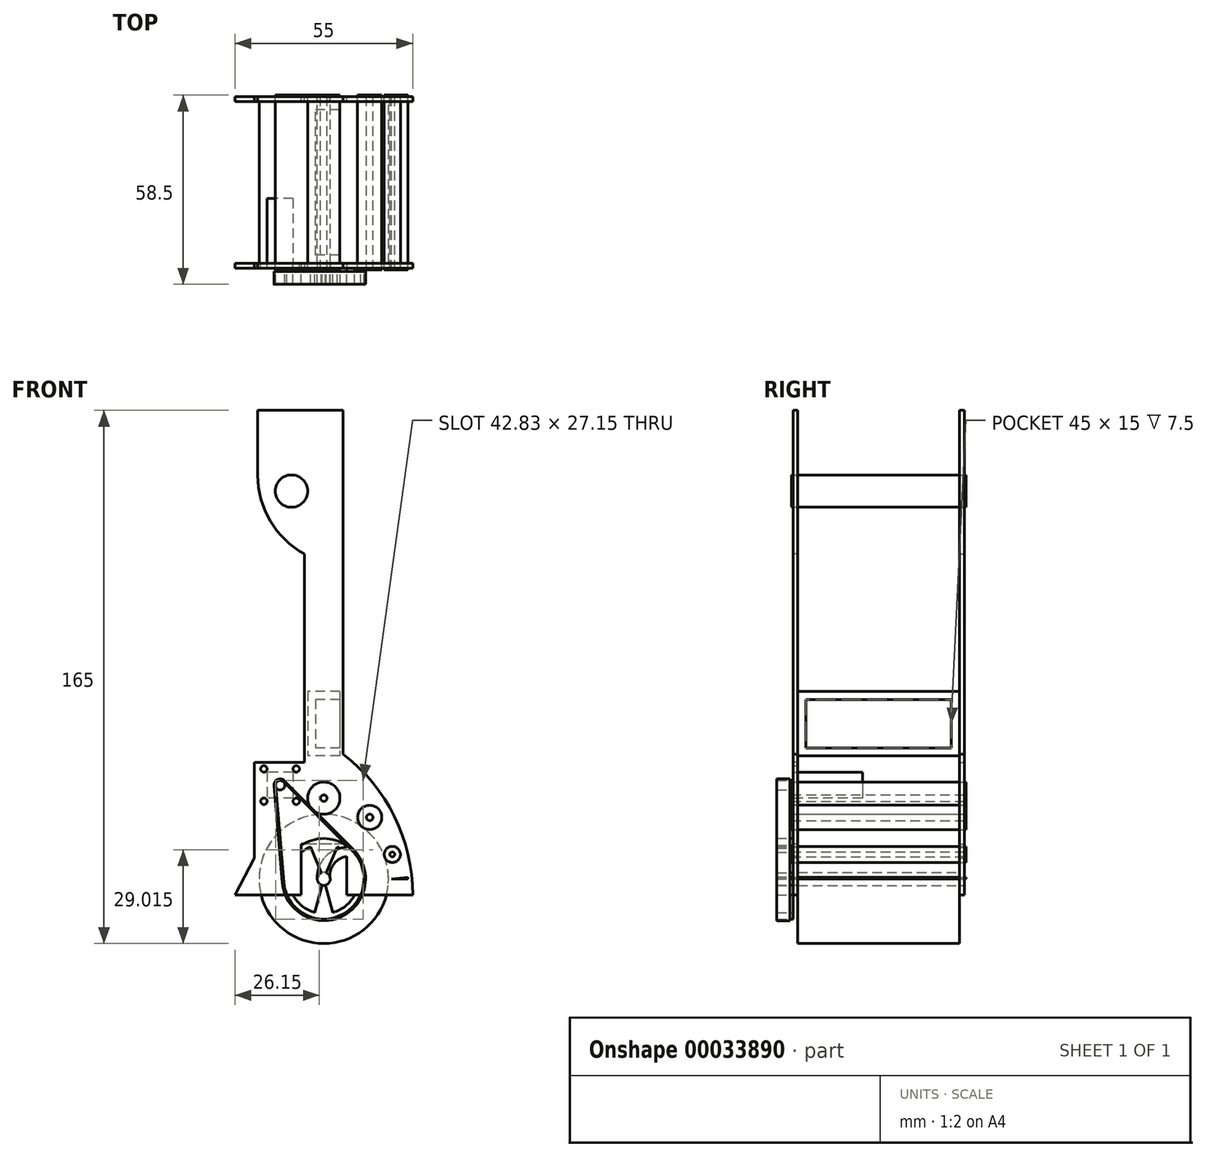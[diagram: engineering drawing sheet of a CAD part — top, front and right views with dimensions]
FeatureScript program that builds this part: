
annotation { "Feature Type Name" : "Feature", "Feature Type Description" : "" }
export const myFeature = defineFeature(function(context is Context, id is Id, definition is map)
    precondition{}
    {
        {
            var Q0;
            Q0=qCreatedBy(makeId("Front.planeOp"),FACE);
            var sketch = newSketch(context, id + "F0", { "sketchPlane" : qUnion([Q0])});
            skCircle(sketch, "E0", {"center": v(0, 0) * mm, "radius": 20 * mm});
            skCircle(sketch, "E1", {"center": v(0, 0) * mm, "radius": 2 * mm});
            skSolve(sketch);
        }
        {
            var Q0;
            Q0=makeQuery(id+"F0.imprint","IMPRINT",FACE,{"disambiguationData":[TD([[makeQuery(id+"F0.imprint","IMPRINT",EDGE,{"derivedFrom":sQuery(id+"F0.wireOp",EDGE,"E0")}),1.0]])]});
            extrude(context, id + "F1", {"entities" : qUnion([Q0]), "endBound" : BoundingType.SYMMETRIC, "depth" : 50 * mm});
        }
        {
            var Q0;
            Q0=qCreatedBy(makeId("Front.planeOp"),FACE);
            var sketch = newSketch(context, id + "F2", { "sketchPlane" : qUnion([Q0])});
            skCircle(sketch, "E2", {"center": v(0, 25) * mm, "radius": 5 * mm});
            skCircle(sketch, "E3", {"center": v(14.2, 19.04) * mm, "radius": 3.75 * mm});
            skCircle(sketch, "E4", {"center": v(21.18, 7.58) * mm, "radius": 2.5 * mm});
            skLineSegment(sketch, "E5", {"start": v(21, 0) * mm, "end": v(26, 0.44) * mm});
            skLineSegment(sketch, "E6", {"start": v(26, 0.44) * mm, "end": v(26, 0) * mm});
            skLineSegment(sketch, "E7", {"start": v(26, 0) * mm, "end": v(21, 0) * mm});
            skCircle(sketch, "E8", {"center": v(0, 25) * mm, "radius": 1 * mm});
            skCircle(sketch, "E9", {"center": v(14.2, 19.04) * mm, "radius": 1 * mm});
            skCircle(sketch, "E10", {"center": v(21.18, 7.58) * mm, "radius": 0.75 * mm});
            skCircle(sketch, "E11", {"center": v(-10, 120) * mm, "radius": 5 * mm});
            skPoint(sketch, "E12.center.orphan", {"position": v(0, 120) * mm});
            skSolve(sketch);
        }
        {
            var Q0;
            Q0=makeQuery(id+"F2.imprint","IMPRINT",FACE,{"disambiguationData":[TD([[makeQuery(id+"F2.imprint","IMPRINT",EDGE,{"derivedFrom":sQuery(id+"F2.wireOp",EDGE,"E2")}),1.0]])]});
            var Q1;
            Q1=makeQuery(id+"F2.imprint","IMPRINT",FACE,{"disambiguationData":[TD([[makeQuery(id+"F2.imprint","IMPRINT",EDGE,{"derivedFrom":sQuery(id+"F2.wireOp",EDGE,"E3")}),1.0]])]});
            var Q2;
            Q2=makeQuery(id+"F2.imprint","IMPRINT",FACE,{"disambiguationData":[TD([[makeQuery(id+"F2.imprint","IMPRINT",EDGE,{"derivedFrom":sQuery(id+"F2.wireOp",EDGE,"E4")}),1.0]])]});
            var Q3;
            Q3=makeQuery(id+"F2.imprint","IMPRINT",FACE,{"disambiguationData":[TD([[makeQuery(id+"F2.imprint","IMPRINT",EDGE,{"derivedFrom":sQuery(id+"F2.wireOp",EDGE,"E5")}),-1.0]])]});
            var Q4;
            Q4=makeQuery(id+"F2.imprint","IMPRINT",FACE,{"disambiguationData":[TD([[makeQuery(id+"F2.imprint","IMPRINT",EDGE,{"derivedFrom":sQuery(id+"F2.wireOp",EDGE,"E11")}),1.0]])]});
            extrude(context, id + "F3", {"entities" : qUnion([Q0, Q1, Q2, Q3, Q4]), "operationType" : NewBodyOperationType.ADD, "endBound" : BoundingType.SYMMETRIC, "depth" : 54 * mm});
        }
        {
            var Q0;
            Q0=qCreatedBy(makeId("Right.planeOp"),FACE);
            var sketch = newSketch(context, id + "F4", { "sketchPlane" : qUnion([Q0])});
            skLineSegment(sketch, "E13.top", {"start": v(-25, 145) * mm, "end": v(-26.5, 145) * mm});
            skLineSegment(sketch, "E13.left", {"start": v(-25, -5) * mm, "end": v(-25, 145) * mm});
            skLineSegment(sketch, "E13.right", {"start": v(-26.5, -5) * mm, "end": v(-26.5, 145) * mm});
            skLineSegment(sketch, "E14", {"start": v(-26.5, -5) * mm, "end": v(-25, -5) * mm});
            skSolve(sketch);
        }
        {
            var Q0;
            Q0=makeQuery(id+"F4.imprint","IMPRINT",FACE,{"disambiguationData":[TD([[makeQuery(id+"F4.imprint","IMPRINT",EDGE,{"derivedFrom":sQuery(id+"F4.wireOp",EDGE,"E13.bottom")}),-1.0]])]});
            var Q1;
            Q1=makeQuery(id+"F4.imprint","IMPRINT",FACE,{"disambiguationData":[TD([[makeQuery(id+"F4.imprint","IMPRINT",EDGE,{"derivedFrom":sQuery(id+"F4.wireOp",EDGE,"E13.top")}),1.0]])]});
            extrude(context, id + "F5", {"entities" : qUnion([Q0, Q1]), "endBound" : BoundingType.SYMMETRIC, "depth" : 55 * mm});
        }
        {
            var Q0;
            Q0=makeQuery(id+"F5.opExtrude","SWEPT_FACE",FACE,{"disambiguationData":[OSD([sQuery(id+"F4.wireOp",EDGE,"E13.right")])]});
            var sketch = newSketch(context, id + "F6", { "sketchPlane" : qUnion([Q0])});
            skLineSegment(sketch, "E15", {"start": v(-82.98, 0) * mm, "end": v(0, 0) * mm, "construction": true});
            skLineSegment(sketch, "E16", {"start": v(-6, 36.03) * mm, "end": v(-6, 100.52) * mm});
            skLineSegment(sketch, "E17", {"start": v(0, 0) * mm, "end": v(0, 66.1) * mm, "construction": true});
            skLineSegment(sketch, "E18", {"start": v(-20.41, 145) * mm, "end": v(-20.41, 124.89) * mm});
            skLineSegment(sketch, "E19", {"start": v(-20.41, 145) * mm, "end": v(6, 145) * mm});
            skLineSegment(sketch, "E20", {"start": v(-27.5, -5) * mm, "end": v(-21.52, 6.42) * mm});
            skLineSegment(sketch, "E21", {"start": v(6, 145) * mm, "end": v(6, 38.62) * mm});
            skArc(sketch, "E22", {"start": v(-20.41, 124.89) * mm, "mid": v(-16.54, 110.73) * mm, "end": v(-6, 100.52) * mm});
            skArc(sketch, "E23", {"start": v(27.5, -5) * mm, "mid": v(21.83, 19.32) * mm, "end": v(6, 38.62) * mm});
            skArc(sketch, "E24", {"start": v(-2, 0) * mm, "mid": v(0, -2) * mm, "end": v(2, 0) * mm});
            skLineSegment(sketch, "E25.trimOffspring", {"start": v(2, 0) * mm, "end": v(98.38, 0) * mm, "construction": true});
            skLineSegment(sketch, "E26", {"start": v(7.08, 0) * mm, "end": v(7.08, 6.96) * mm});
            skLineSegment(sketch, "E27", {"start": v(7.08, 10.84) * mm, "end": v(-6.96, 10.84) * mm});
            skLineSegment(sketch, "E28", {"start": v(-6.96, 10.84) * mm, "end": v(-6.96, 0) * mm});
            skArc(sketch, "E29", {"start": v(7.08, 6.96) * mm, "mid": v(3.06, 4.56) * mm, "end": v(2, 0) * mm});
            skArc(sketch, "E30", {"start": v(7.08, 9.77) * mm, "mid": v(0.47, 6.81) * mm, "end": v(-2, 0) * mm});
            skLineSegment(sketch, "E31", {"start": v(-6.96, 0) * mm, "end": v(-6.96, -5) * mm});
            skLineSegment(sketch, "E32", {"start": v(-6.96, -5) * mm, "end": v(7.08, -5) * mm});
            skLineSegment(sketch, "E33", {"start": v(7.08, 0) * mm, "end": v(7.08, -5) * mm});
            skLineSegment(sketch, "E34.trimOffspring", {"start": v(7.08, 9.77) * mm, "end": v(7.08, 10.84) * mm});
            skLineSegment(sketch, "E35", {"start": v(-6, 36.03) * mm, "end": v(-21.52, 36.03) * mm});
            skLineSegment(sketch, "E36", {"start": v(-21.52, 36.03) * mm, "end": v(-21.52, 6.42) * mm});
            skSolve(sketch);
        }
        {
            var Q0;
            Q0=makeQuery(id+"F6.imprint","IMPRINT",FACE,{"disambiguationData":[TD([[makeQuery(id+"F6.imprint","IMPRINT",EDGE,{"derivedFrom":sQuery(id+"F6.wireOp",EDGE,"E16")}),1.0]])]});
            var Q1;
            {var subQ2=sQuery(id+"F6.wireOp",EDGE,"E21");Q1=makeQuery(id+"F6.imprint","IMPRINT",FACE,{"disambiguationData":[TD([[makeQuery(id+"F6.imprint","IMPRINT",EDGE,{"derivedFrom":subQ2}),1.0]])]});}
            var Q2;
            Q2=makeQuery(id+"F6.imprint","IMPRINT",FACE,{"disambiguationData":[TD([[makeQuery(id+"F6.imprint","IMPRINT",EDGE,{"derivedFrom":sQuery(id+"F6.wireOp",EDGE,"E24")}),-1.0]])]});
            extrude(context, id + "F7", {"entities" : qUnion([Q0, Q1, Q2]), "operationType" : NewBodyOperationType.REMOVE, "oppositeDirection" : true, "depth" : 1.5 * mm});
        }
        {
            var Q0;
            Q0=makeQuery(id+"F5.opExtrude","SWEPT_BODY",BODY,{"disambiguationData":[OSD([sQuery(id+"F4.wireOp",EDGE,"E13.bottom"),sQuery(id+"F4.wireOp",EDGE,"E13.top"),sQuery(id+"F4.wireOp",EDGE,"E13.left"),sQuery(id+"F4.wireOp",EDGE,"E13.right")])]});
            var Q1;
            Q1=qCreatedBy(makeId("Front.planeOp"),FACE);
            mirror(context, id + "F8", {"entities" : qUnion([Q0]), "mirrorPlane" : qUnion([Q1])});
        }
        {
            var Q0;
            Q0=makeQuery(id+"F5.opExtrude","SWEPT_FACE",FACE,{"disambiguationData":[OSD([sQuery(id+"F4.wireOp",EDGE,"E13.left")])]});
            var sketch = newSketch(context, id + "F9", { "sketchPlane" : qUnion([Q0])});
            skCircle(sketch, "E37", {"center": v(8.52, 34.03) * mm, "radius": 1 * mm});
            skCircle(sketch, "E38", {"center": v(18.52, 34.03) * mm, "radius": 1 * mm});
            skCircle(sketch, "E39", {"center": v(8.52, 24.03) * mm, "radius": 1 * mm});
            skCircle(sketch, "E40", {"center": v(18.52, 24.03) * mm, "radius": 1 * mm});
            skLineSegment(sketch, "E41", {"start": v(18.52, 34.03) * mm, "end": v(18.52, 24.03) * mm, "construction": true});
            skLineSegment(sketch, "E42", {"start": v(8.52, 34.03) * mm, "end": v(8.52, 24.03) * mm, "construction": true});
            skLineSegment(sketch, "E43.bottom", {"start": v(9.52, 33.03) * mm, "end": v(17.52, 33.03) * mm});
            skLineSegment(sketch, "E43.top", {"start": v(9.52, 25.03) * mm, "end": v(17.52, 25.03) * mm});
            skLineSegment(sketch, "E43.left", {"start": v(9.52, 33.03) * mm, "end": v(9.52, 25.03) * mm});
            skLineSegment(sketch, "E43.right", {"start": v(17.52, 33.03) * mm, "end": v(17.52, 25.03) * mm});
            skLineSegment(sketch, "E44", {"start": v(8.52, 34.03) * mm, "end": v(18.52, 34.03) * mm, "construction": true});
            skSolve(sketch);
        }
        {
            var Q0;
            Q0=makeQuery(id+"F9.imprint","IMPRINT",FACE,{"disambiguationData":[TD([[makeQuery(id+"F9.imprint","IMPRINT",EDGE,{"derivedFrom":sQuery(id+"F9.wireOp",EDGE,"E43.bottom")}),-1.0]])]});
            extrude(context, id + "F10", {"entities" : qUnion([Q0]), "depth" : 20 * mm});
        }
        {
            var Q0;
            Q0=makeQuery(id+"F9.imprint","IMPRINT",FACE,{"disambiguationData":[TD([[makeQuery(id+"F9.imprint","IMPRINT",EDGE,{"derivedFrom":sQuery(id+"F9.wireOp",EDGE,"E37")}),-1.0]])]});
            var sketch = newSketch(context, id + "F11", { "sketchPlane" : qUnion([Q0])});
            skCircle(sketch, "E45", {"center": v(8.52, 34.03) * mm, "radius": 1 * mm});
            skCircle(sketch, "E46", {"center": v(18.52, 34.03) * mm, "radius": 1 * mm});
            skCircle(sketch, "E47", {"center": v(8.52, 24.03) * mm, "radius": 1 * mm});
            skCircle(sketch, "E48", {"center": v(18.52, 24.03) * mm, "radius": 1 * mm});
            skSolve(sketch);
        }
        {
            var Q0;
            Q0 = qSketchRegion(id + "F11", true);
            extrude(context, id + "F12", {"entities" : qUnion([Q0]), "operationType" : NewBodyOperationType.REMOVE, "endBound" : BoundingType.THROUGH_ALL, "oppositeDirection" : true, "depth" : 25 * mm});
        }
        {
            var Q0;
            Q0=makeQuery(id+"F5.opExtrude","SWEPT_FACE",FACE,{"disambiguationData":[OSD([sQuery(id+"F4.wireOp",EDGE,"E13.right")])]});
            var sketch = newSketch(context, id + "F13", { "sketchPlane" : qUnion([Q0])});
            skCircle(sketch, "E49", {"center": v(-13.52, 29.03) * mm, "radius": 1.5 * mm});
            skLineSegment(sketch, "E50", {"start": v(-18.52, 24.03) * mm, "end": v(-8.52, 34.03) * mm, "construction": true});
            skLineSegment(sketch, "E51", {"start": v(-18.52, 34.03) * mm, "end": v(-8.52, 24.03) * mm, "construction": true});
            skCircle(sketch, "E52", {"center": v(0, 0) * mm, "radius": 12.5 * mm});
            skArc(sketch, "E53", {"start": v(-4.11, 9.93) * mm, "mid": v(-10.73, -0.69) * mm, "end": v(-2.82, -10.38) * mm});
            skCircle(sketch, "E54", {"center": v(0, 0) * mm, "radius": 2.01 * mm});
            skLineSegment(sketch, "E55", {"start": v(0.77, 1.86) * mm, "end": v(4.11, 9.93) * mm});
            skLineSegment(sketch, "E56", {"start": v(-0.77, 1.86) * mm, "end": v(-4.11, 9.93) * mm});
            skLineSegment(sketch, "E57", {"start": v(-0.52, -1.93) * mm, "end": v(-2.82, -10.38) * mm});
            skLineSegment(sketch, "E58", {"start": v(0.52, -1.93) * mm, "end": v(2.82, -10.38) * mm});
            skLineSegment(sketch, "E59", {"start": v(0, 0) * mm, "end": v(0, 9.4) * mm, "construction": true});
            skArc(sketch, "E60.trimOffspring", {"start": v(2.82, -10.38) * mm, "mid": v(10.73, -0.69) * mm, "end": v(4.11, 9.93) * mm});
            skSolve(sketch);
        }
        {
            var Q0;
            Q0=makeQuery(id+"F13.imprint","IMPRINT",FACE,{"disambiguationData":[TD([[makeQuery(id+"F13.imprint","IMPRINT",EDGE,{"derivedFrom":sQuery(id+"F13.wireOp",EDGE,"E49")}),1.0]])]});
            var Q1;
            {var subQ2=sQuery(id+"F6.wireOp",EDGE,"E28");var subQ3=sQuery(id+"F6.wireOp",EDGE,"E31");var subQ7=sQuery(id+"F13.wireOp",EDGE,"E52");var subQ9=makeQuery(id+"F7.boolean.opBoolean","COPY",EDGE,{"derivedFrom":makeQuery(id+"F7.opExtrude","CAP_EDGE",EDGE,{"disambiguationData":[OSD([subQ2,subQ3])],"isStart":true})});var subQ11=makeQuery(id+"F13.imprint","INTERSECT",VERTEX,{"derivedFrom":[subQ9,subQ7]});Q1=makeQuery(id+"F13.imprint","IMPRINT",FACE,{"disambiguationData":[TD([[makeQuery(id+"F13.imprint","IMPRINT",EDGE,{"disambiguationData":[TD([[subQ11,-1.0]])],"derivedFrom":subQ9}),-1.0]])]});}
            var Q2;
            {var subQ16=sQuery(id+"F13.wireOp",EDGE,"E54");var subQ18=sQuery(id+"F13.wireOp",EDGE,"E57");var subQ19=makeQuery(id+"F13.imprint","INTERSECT",VERTEX,{"derivedFrom":[subQ16,subQ18]});Q2=makeQuery(id+"F13.imprint","IMPRINT",FACE,{"disambiguationData":[TD([[makeQuery(id+"F13.imprint","IMPRINT",EDGE,{"disambiguationData":[TD([[subQ19,-1.0]])],"derivedFrom":subQ16}),-1.0]])]});}
            var Q3;
            {var subQ7=makeQuery(id+"F7.boolean.opBoolean","COPY",EDGE,{"derivedFrom":makeQuery(id+"F7.opExtrude","CAP_EDGE",EDGE,{"disambiguationData":[OSD([sQuery(id+"F6.wireOp",EDGE,"E34.trimOffspring")])],"isStart":true})});var subQ9=makeQuery(id+"F7.boolean.opBoolean","COPY",EDGE,{"derivedFrom":makeQuery(id+"F7.opExtrude","CAP_EDGE",EDGE,{"disambiguationData":[OSD([sQuery(id+"F6.wireOp",EDGE,"E30")])],"isStart":true})});var subQ10=makeQuery(id+"F13.imprint","INTERSECT",VERTEX,{"derivedFrom":[subQ9,subQ7]});Q3=makeQuery(id+"F13.imprint","IMPRINT",FACE,{"disambiguationData":[TD([[makeQuery(id+"F13.imprint","IMPRINT",EDGE,{"disambiguationData":[TD([[subQ10,-1.0]])],"derivedFrom":subQ9}),1.0]])]});}
            var Q4;
            {var subQ0=makeQuery(id+"F7.boolean.opBoolean","COPY",EDGE,{"derivedFrom":makeQuery(id+"F7.opExtrude","CAP_EDGE",EDGE,{"disambiguationData":[OSD([sQuery(id+"F6.wireOp",EDGE,"E27")])],"isStart":true})});var subQ1=sQuery(id+"F13.wireOp",EDGE,"E52");var subQ3=makeQuery(id+"F13.imprint","INTERSECT",VERTEX,{"disambiguationData":[OD(0.0)],"derivedFrom":[subQ0,subQ1]});Q4=makeQuery(id+"F13.imprint","IMPRINT",FACE,{"disambiguationData":[TD([[makeQuery(id+"F13.imprint","IMPRINT",EDGE,{"disambiguationData":[TD([[subQ3,-1.0]])],"derivedFrom":subQ1}),1.0]])]});}
            var Q5;
            {var subQ6=sQuery(id+"F13.wireOp",EDGE,"E52");var subQ16=makeQuery(id+"F7.boolean.opBoolean","COPY",EDGE,{"derivedFrom":makeQuery(id+"F7.opExtrude","CAP_EDGE",EDGE,{"disambiguationData":[OSD([sQuery(id+"F6.wireOp",EDGE,"E27")])],"isStart":true})});var subQ18=makeQuery(id+"F13.imprint","INTERSECT",VERTEX,{"disambiguationData":[OD(0.0)],"derivedFrom":[subQ16,subQ6]});Q5=makeQuery(id+"F13.imprint","IMPRINT",FACE,{"disambiguationData":[TD([[makeQuery(id+"F13.imprint","IMPRINT",EDGE,{"disambiguationData":[TD([[subQ18,1.0]])],"derivedFrom":subQ6}),1.0]])]});}
            var Q6;
            {var subQ3=sQuery(id+"F13.wireOp",EDGE,"E55");var subQ5=sQuery(id+"F13.wireOp",EDGE,"E54");var subQ7=makeQuery(id+"F13.imprint","INTERSECT",VERTEX,{"derivedFrom":[subQ5,subQ3]});Q6=makeQuery(id+"F13.imprint","IMPRINT",FACE,{"disambiguationData":[TD([[makeQuery(id+"F13.imprint","IMPRINT",EDGE,{"disambiguationData":[TD([[subQ7,-1.0]])],"derivedFrom":subQ5}),-1.0]])]});}
            var Q7;
            {var subQ1=sQuery(id+"F13.wireOp",EDGE,"E54");var subQ11=makeQuery(id+"F13.imprint","INTERSECT",VERTEX,{"derivedFrom":[subQ1,sQuery(id+"F13.wireOp",EDGE,"E55")]});Q7=makeQuery(id+"F13.imprint","IMPRINT",FACE,{"disambiguationData":[TD([[makeQuery(id+"F13.imprint","IMPRINT",EDGE,{"disambiguationData":[TD([[subQ11,1.0]])],"derivedFrom":subQ1}),1.0]])]});}
            extrude(context, id + "F14", {"entities" : qUnion([Q0, Q1, Q2, Q3, Q4, Q5, Q6, Q7]), "depth" : 5 * mm});
        }
        {
            var Q0;
            Q0=makeQuery(id+"F5.opExtrude","SWEPT_FACE",FACE,{"disambiguationData":[OSD([sQuery(id+"F4.wireOp",EDGE,"E13.right")])]});
            var sketch = newSketch(context, id + "F15", { "sketchPlane" : qUnion([Q0])});
            skLineSegment(sketch, "E61", {"start": v(-12.46, 30.1) * mm, "end": v(8.83, 8.85) * mm});
            skLineSegment(sketch, "E62", {"start": v(-12.45, -1.06) * mm, "end": v(-15.01, 28.9) * mm});
            skArc(sketch, "E63", {"start": v(-12.45, -1.06) * mm, "mid": v(5.28, -11.33) * mm, "end": v(8.83, 8.85) * mm});
            skArc(sketch, "E64", {"start": v(-12.46, 30.1) * mm, "mid": v(-14.15, 30.4) * mm, "end": v(-15.01, 28.9) * mm});
            skSolve(sketch);
        }
        {
            var Q0;
            Q0=sQuery(id+"F15.wireOp",VERTEX,"E64.center");
            var Q1;
            Q1=qCreatedBy(makeId("Right.planeOp"),FACE);
            cPlane(context, id + "F16", {"entities" : qUnion([Q0, Q1]), "cplaneType" : CPlaneType.PLANE_POINT, "offset" : 150 * mm, "width" : 150 * mm, "height" : 150 * mm});
        }
        {
            var Q0;
            Q0=qCreatedBy(id+"F16.planeOp",FACE);
            var sketch = newSketch(context, id + "F17", { "sketchPlane" : qUnion([Q0])});
            skLineSegment(sketch, "E65.top", {"start": v(-31.5, 30.44) * mm, "end": v(-27.5, 30.44) * mm});
            skLineSegment(sketch, "E65.left", {"start": v(-31.5, 30.94) * mm, "end": v(-31.5, 30.44) * mm});
            skLineSegment(sketch, "E65.right", {"start": v(-27.5, 30.94) * mm, "end": v(-27.5, 30.44) * mm});
            skLineSegment(sketch, "E66", {"start": v(-31.5, 30.94) * mm, "end": v(-27.5, 30.94) * mm});
            skSolve(sketch);
        }
        {
            var Q0;
            Q0 = qSketchRegion(id + "F17", true);
            var Q1;
            Q1 = qConstructionFilter(qBodyType(qCreatedBy(id + "F15" ,EDGE), BodyType.WIRE), ConstructionObject.NO);
            sweep(context, id + "F18", {"profiles" : qUnion([Q0]), "path" : qUnion([Q1])});
        }
        {
            var Q0;
            Q0=qCreatedBy(makeId("Right.planeOp"),FACE);
            var sketch = newSketch(context, id + "F19", { "sketchPlane" : qUnion([Q0])});
            skLineSegment(sketch, "E67.bottom", {"start": v(-25, 58.03) * mm, "end": v(25, 58.03) * mm});
            skLineSegment(sketch, "E67.top", {"start": v(-25, 38.03) * mm, "end": v(25, 38.03) * mm});
            skLineSegment(sketch, "E67.left", {"start": v(-25, 58.03) * mm, "end": v(-25, 38.03) * mm});
            skLineSegment(sketch, "E67.right", {"start": v(25, 58.03) * mm, "end": v(25, 38.03) * mm});
            skSolve(sketch);
        }
        {
            var Q0;
            Q0=makeQuery(id+"F19.imprint","IMPRINT",FACE,{"disambiguationData":[TD([[makeQuery(id+"F19.imprint","IMPRINT",EDGE,{"derivedFrom":sQuery(id+"F19.wireOp",EDGE,"E67.bottom")}),-1.0]])]});
            extrude(context, id + "F20", {"entities" : qUnion([Q0]), "endBound" : BoundingType.SYMMETRIC, "depth" : 10 * mm});
        }
        {
            var Q0;
            Q0=makeQuery(id+"F20.opExtrude","CAP_FACE",FACE,{"disambiguationData":[OSD([sQuery(id+"F19.wireOp",EDGE,"E67.bottom"),sQuery(id+"F19.wireOp",EDGE,"E67.top"),sQuery(id+"F19.wireOp",EDGE,"E67.left"),sQuery(id+"F19.wireOp",EDGE,"E67.right")])],"isStart":false});
            shell(context, id + "F21", {"entities" : qUnion([Q0]), "thickness" : 2.5 * mm});
        }
    });
